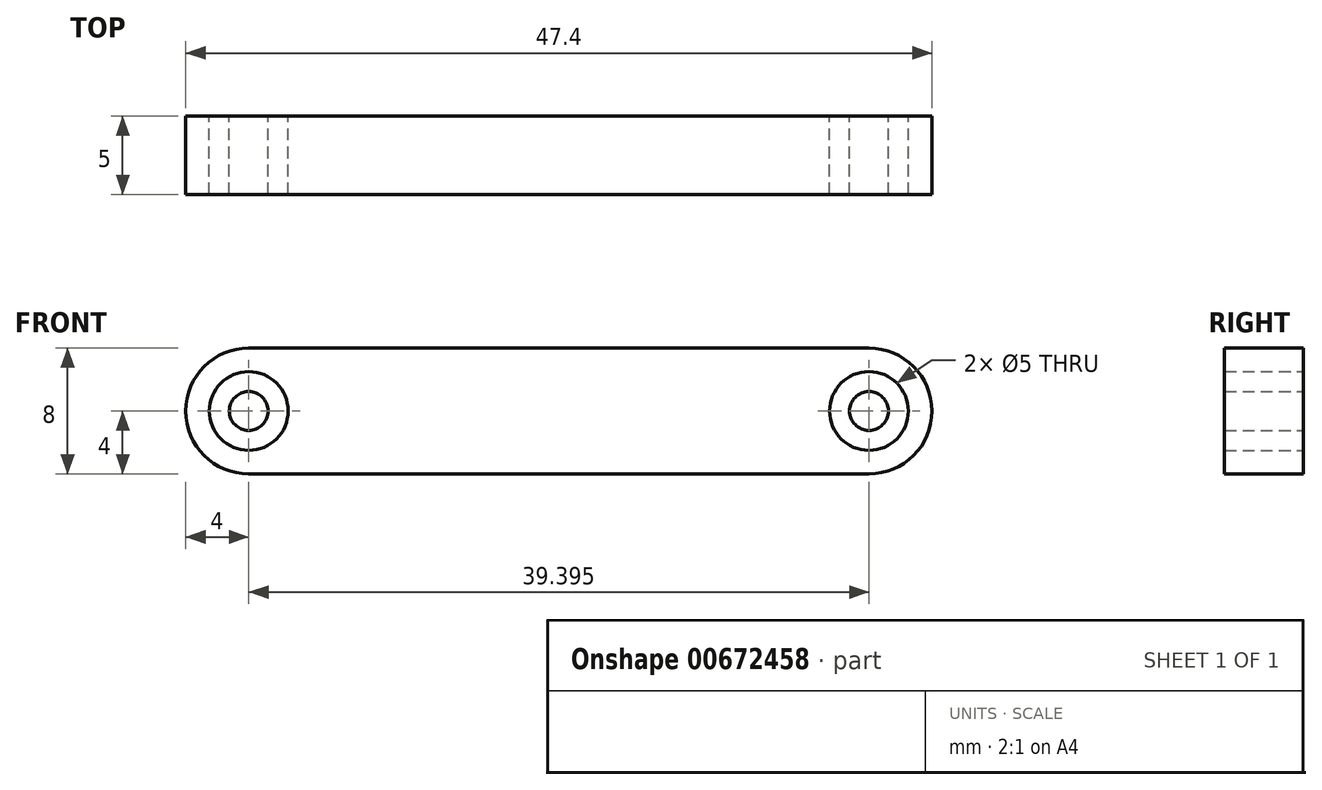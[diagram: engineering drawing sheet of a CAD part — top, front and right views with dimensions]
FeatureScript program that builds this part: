
annotation { "Feature Type Name" : "Feature", "Feature Type Description" : "" }
export const myFeature = defineFeature(function(context is Context, id is Id, definition is map)
    precondition{}
    {
        {
            var Q0;
            Q0=qCreatedBy(makeId("Front.planeOp"),FACE);
            var sketch = newSketch(context, id + "F0", { "sketchPlane" : qUnion([Q0])});
            skArc(sketch, "E0", {"start": v(0, 4) * mm, "mid": v(-4, 0) * mm, "end": v(0, -4) * mm});
            skCircle(sketch, "E1", {"center": v(0, 0) * mm, "radius": 2.5 * mm});
            skArc(sketch, "E2", {"start": v(39.4, -4) * mm, "mid": v(43.4, 0) * mm, "end": v(39.4, 4) * mm});
            skCircle(sketch, "E3", {"center": v(39.4, 0) * mm, "radius": 2.5 * mm});
            skLineSegment(sketch, "E4", {"start": v(0, 4) * mm, "end": v(39.4, 4) * mm});
            skLineSegment(sketch, "E5", {"start": v(0, -4) * mm, "end": v(39.4, -4) * mm});
            skCircle(sketch, "E6", {"center": v(0, 0) * mm, "radius": 1.23 * mm});
            skCircle(sketch, "E7", {"center": v(39.4, 0) * mm, "radius": 1.23 * mm});
            skSolve(sketch);
        }
        {
            var Q0;
            Q0=makeQuery(id+"F0.imprint","IMPRINT",FACE,{"disambiguationData":[TD([[makeQuery(id+"F0.imprint","IMPRINT",EDGE,{"derivedFrom":sQuery(id+"F0.wireOp",EDGE,"E0")}),1.0]])]});
            var Q1;
            Q1=makeQuery(id+"F0.imprint","IMPRINT",FACE,{"disambiguationData":[TD([[makeQuery(id+"F0.imprint","IMPRINT",EDGE,{"derivedFrom":sQuery(id+"F0.wireOp",EDGE,"E6")}),1.0]])]});
            var Q2;
            Q2=makeQuery(id+"F0.imprint","IMPRINT",FACE,{"disambiguationData":[TD([[makeQuery(id+"F0.imprint","IMPRINT",EDGE,{"derivedFrom":sQuery(id+"F0.wireOp",EDGE,"E7")}),1.0]])]});
            extrude(context, id + "F1", {"entities" : qUnion([Q0, Q1, Q2]), "endBound" : BoundingType.SYMMETRIC, "depth" : 5 * mm, "offsetDistance" : 25.4 * mm});
        }
    });
